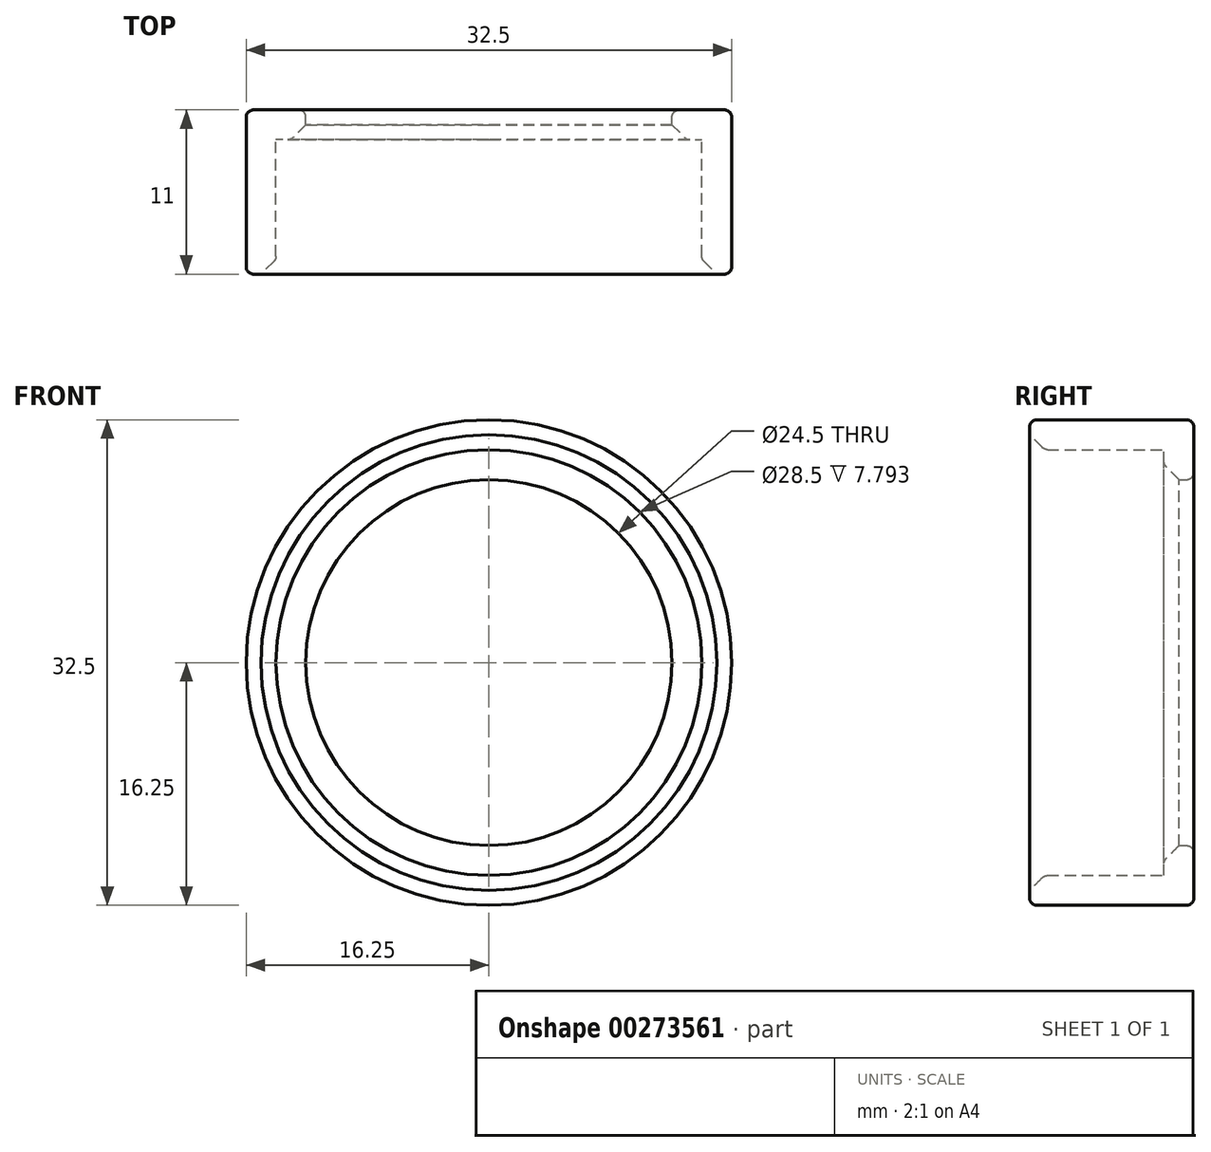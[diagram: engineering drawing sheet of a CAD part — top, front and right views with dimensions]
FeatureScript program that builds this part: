
annotation { "Feature Type Name" : "Feature", "Feature Type Description" : "" }
export const myFeature = defineFeature(function(context is Context, id is Id, definition is map)
    precondition{}
    {
        {
            var Q0;
            Q0=qCreatedBy(makeId("Front.planeOp"),FACE);
            var sketch = newSketch(context, id + "F0", { "sketchPlane" : qUnion([Q0])});
            skCircle(sketch, "E0", {"center": v(0, 0) * mm, "radius": 14.25 * mm});
            skCircle(sketch, "E1.0", {"center": v(0, 0) * mm, "radius": 16.25 * mm});
            skCircle(sketch, "E2.0", {"center": v(0, 0) * mm, "radius": 12.25 * mm});
            skSolve(sketch);
        }
        {
            var Q0;
            Q0=makeQuery(id+"F0.imprint","IMPRINT",FACE,{"disambiguationData":[TD([[makeQuery(id+"F0.imprint","IMPRINT",EDGE,{"derivedFrom":sQuery(id+"F0.wireOp",EDGE,"E0")}),1.0]])]});
            var Q1;
            Q1=makeQuery(id+"F0.imprint","IMPRINT",FACE,{"disambiguationData":[TD([[makeQuery(id+"F0.imprint","IMPRINT",EDGE,{"derivedFrom":sQuery(id+"F0.wireOp",EDGE,"E0")}),-1.0]])]});
            extrude(context, id + "F1", {"entities" : qUnion([Q0, Q1]), "depth" : 2 * mm});
        }
        {
            var Q0;
            Q0=makeQuery(id+"F0.imprint","IMPRINT",FACE,{"disambiguationData":[TD([[makeQuery(id+"F0.imprint","IMPRINT",EDGE,{"derivedFrom":sQuery(id+"F0.wireOp",EDGE,"E0")}),-1.0]])]});
            extrude(context, id + "F2", {"entities" : qUnion([Q0]), "operationType" : NewBodyOperationType.ADD, "depth" : 11 * mm});
        }
        {
            var Q0;
            Q0=makeQuery(id+"F2.opExtrude","CAP_EDGE",EDGE,{"disambiguationData":[OSD([sQuery(id+"F0.wireOp",EDGE,"E0")])],"isStart":false});
            var Q1;
            Q1=makeQuery(id+"F1.opExtrude","CAP_EDGE",EDGE,{"disambiguationData":[OSD([sQuery(id+"F0.wireOp",EDGE,"E2.0")])],"isStart":false});
            chamfer(context, id + "F3", {"entities" : qUnion([Q0, Q1]), "width" : 1 * mm, "tangentPropagation" : true});
        }
        {
            var Q0;
            {var subQ0=sQuery(id+"F0.wireOp",EDGE,"E1.0");Q0=makeQuery(id+"F2.boolean.opBoolean","MERGE",FACE,{"derivedFrom":[makeQuery(id+"F1.opExtrude","SWEPT_FACE",FACE,{"disambiguationData":[OSD([subQ0])]}),makeQuery(id+"F2.opExtrude","SWEPT_FACE",FACE,{"disambiguationData":[OSD([subQ0])]})]});}
            var Q1;
            Q1=makeQuery(id+"F1.opExtrude","CAP_EDGE",EDGE,{"disambiguationData":[OSD([sQuery(id+"F0.wireOp",EDGE,"E2.0")])],"isStart":true});
            var Q2;
            {var subQ0=sQuery(id+"F0.wireOp",EDGE,"E0");Q2=makeQuery(id+"F3.opChamfer","BLEND_EDGE",EDGE,{"blendedFrom":[makeQuery(id+"F2.opExtrude","CAP_EDGE",EDGE,{"disambiguationData":[OSD([subQ0])],"isStart":false}),makeQuery(id+"F2.opExtrude","SWEPT_FACE",FACE,{"disambiguationData":[OSD([subQ0])]})],"blendedInto":[makeQuery(id+"F2.opExtrude","SWEPT_FACE",FACE,{"disambiguationData":[OSD([subQ0])]})]});}
            var Q3;
            {var subQ0=sQuery(id+"F0.wireOp",EDGE,"E2.0");Q3=makeQuery(id+"F3.opChamfer","BLEND_EDGE",EDGE,{"blendedFrom":[makeQuery(id+"F1.opExtrude","CAP_EDGE",EDGE,{"disambiguationData":[OSD([subQ0])],"isStart":false}),makeQuery(id+"F1.opExtrude","CAP_FACE",FACE,{"disambiguationData":[OSD([sQuery(id+"F0.wireOp",EDGE,"E1.0"),subQ0])],"isStart":false})],"blendedInto":[makeQuery(id+"F1.opExtrude","CAP_FACE",FACE,{"disambiguationData":[OSD([sQuery(id+"F0.wireOp",EDGE,"E1.0"),subQ0])],"isStart":false})]});}
            fillet(context, id + "F4", {"entities" : qUnion([Q0, Q1, Q2, Q3]), "radius" : .5 * mm, "tangentPropagation" : true, "allowEdgeOverflow" : false});
        }
    });
